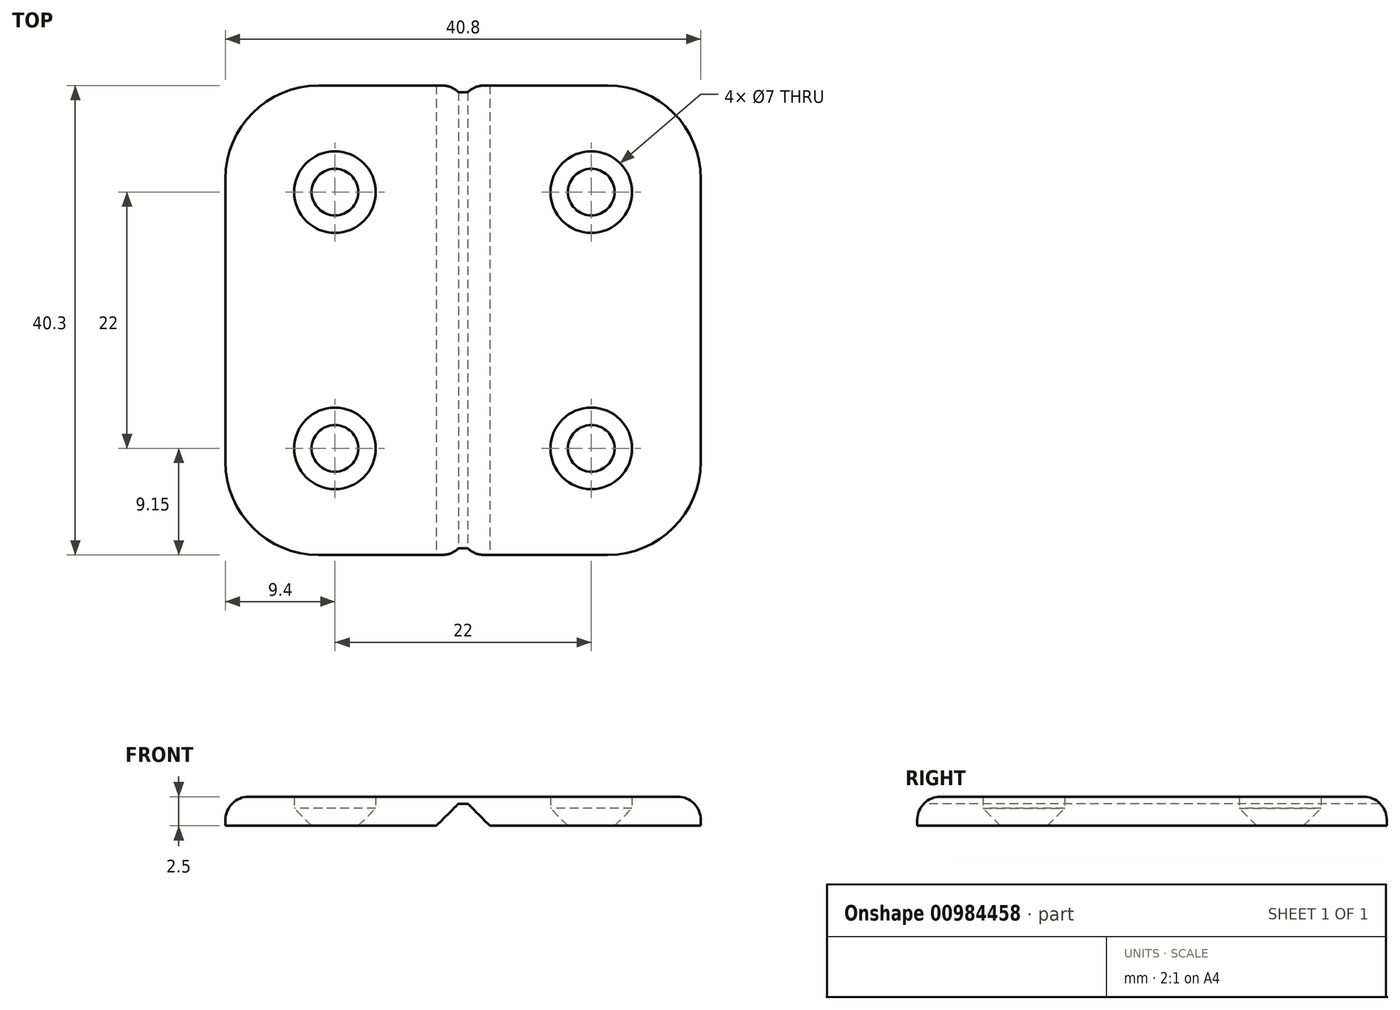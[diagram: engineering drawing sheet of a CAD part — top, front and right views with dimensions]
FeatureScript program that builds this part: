
annotation { "Feature Type Name" : "Feature", "Feature Type Description" : "" }
export const myFeature = defineFeature(function(context is Context, id is Id, definition is map)
    precondition{}
    {
        {
            var Q0;
            Q0=qCreatedBy(makeId("Top.planeOp"),FACE);
            var sketch = newSketch(context, id + "F0", { "sketchPlane" : qUnion([Q0])});
            skLineSegment(sketch, "E0.bottom", {"start": v(12.4, 20.15) * mm, "end": v(-12.4, 20.15) * mm});
            skLineSegment(sketch, "E0.top", {"start": v(12.4, -20.15) * mm, "end": v(-12.4, -20.15) * mm});
            skLineSegment(sketch, "E0.left", {"start": v(20.4, 12.15) * mm, "end": v(20.4, -12.15) * mm});
            skLineSegment(sketch, "E0.right", {"start": v(-20.4, 12.15) * mm, "end": v(-20.4, -12.15) * mm});
            skPoint(sketch, "E0.middle", {"position": v(0, 0) * mm});
            skPoint(sketch, "E1.visualSharp", {"position": v(-20.4, 20.15) * mm});
            skArc(sketch, "E1.filletArc", {"start": v(-12.4, 20.15) * mm, "mid": v(-18.06, 17.8) * mm, "end": v(-20.4, 12.15) * mm});
            skPoint(sketch, "E2.visualSharp", {"position": v(20.4, 20.15) * mm});
            skArc(sketch, "E2.filletArc", {"start": v(20.4, 12.15) * mm, "mid": v(18.06, 17.8) * mm, "end": v(12.4, 20.15) * mm});
            skPoint(sketch, "E3.visualSharp", {"position": v(20.4, -20.15) * mm});
            skArc(sketch, "E3.filletArc", {"start": v(12.4, -20.15) * mm, "mid": v(18.06, -17.8) * mm, "end": v(20.4, -12.15) * mm});
            skPoint(sketch, "E4.visualSharp", {"position": v(-20.4, -20.15) * mm});
            skArc(sketch, "E4.filletArc", {"start": v(-20.4, -12.15) * mm, "mid": v(-18.06, -17.8) * mm, "end": v(-12.4, -20.15) * mm});
            skCircle(sketch, "E5", {"center": v(11, 11) * mm, "radius": 2 * mm});
            skCircle(sketch, "E6", {"center": v(11, -11) * mm, "radius": 2 * mm});
            skCircle(sketch, "E7", {"center": v(-11, -11) * mm, "radius": 2 * mm});
            skCircle(sketch, "E8", {"center": v(-11, 11) * mm, "radius": 2 * mm});
            skCircle(sketch, "E9", {"center": v(-11, 11) * mm, "radius": 3.5 * mm});
            skCircle(sketch, "E10", {"center": v(11, 11) * mm, "radius": 3.5 * mm});
            skCircle(sketch, "E11", {"center": v(-11, -11) * mm, "radius": 3.5 * mm});
            skCircle(sketch, "E12", {"center": v(11, -11) * mm, "radius": 3.5 * mm});
            skSolve(sketch);
        }
        {
            var Q0;
            Q0=makeQuery(id+"F0.imprint","IMPRINT",FACE,{"disambiguationData":[TD([[makeQuery(id+"F0.imprint","IMPRINT",EDGE,{"derivedFrom":sQuery(id+"F0.wireOp",EDGE,"E0.bottom")}),1.0]])]});
            var Q1;
            Q1=makeQuery(id+"F0.imprint","IMPRINT",FACE,{"disambiguationData":[TD([[makeQuery(id+"F0.imprint","IMPRINT",EDGE,{"derivedFrom":sQuery(id+"F0.wireOp",EDGE,"E8")}),-1.0]])]});
            var Q2;
            Q2=makeQuery(id+"F0.imprint","IMPRINT",FACE,{"disambiguationData":[TD([[makeQuery(id+"F0.imprint","IMPRINT",EDGE,{"derivedFrom":sQuery(id+"F0.wireOp",EDGE,"E5")}),-1.0]])]});
            var Q3;
            Q3=makeQuery(id+"F0.imprint","IMPRINT",FACE,{"disambiguationData":[TD([[makeQuery(id+"F0.imprint","IMPRINT",EDGE,{"derivedFrom":sQuery(id+"F0.wireOp",EDGE,"E6")}),-1.0]])]});
            var Q4;
            Q4=makeQuery(id+"F0.imprint","IMPRINT",FACE,{"disambiguationData":[TD([[makeQuery(id+"F0.imprint","IMPRINT",EDGE,{"derivedFrom":sQuery(id+"F0.wireOp",EDGE,"E7")}),-1.0]])]});
            extrude(context, id + "F1", {"entities" : qUnion([Q0, Q1, Q2, Q3, Q4]), "depth" : 1.5 * mm, "offsetDistance" : 25 * mm});
        }
        {
            var Q0;
            Q0=makeQuery(id+"F0.imprint","IMPRINT",FACE,{"disambiguationData":[TD([[makeQuery(id+"F0.imprint","IMPRINT",EDGE,{"derivedFrom":sQuery(id+"F0.wireOp",EDGE,"E0.bottom")}),1.0]])]});
            extrude(context, id + "F2", {"entities" : qUnion([Q0]), "operationType" : NewBodyOperationType.ADD, "depth" : 2.5 * mm, "offsetDistance" : 25 * mm});
        }
        {
            var Q0;
            Q0=makeQuery(id+"F2.opExtrude","CAP_EDGE",EDGE,{"disambiguationData":[OSD([sQuery(id+"F0.wireOp",EDGE,"E1.filletArc")])],"isStart":false});
            fillet(context, id + "F3", {"entities" : qUnion([Q0]), "radius" : 2 * mm, "tangentPropagation" : true, "allowEdgeOverflow" : false});
        }
        {
            var Q0;
            Q0=makeQuery(id+"F1.opExtrude","CAP_EDGE",EDGE,{"disambiguationData":[OSD([sQuery(id+"F0.wireOp",EDGE,"E8")])],"isStart":false});
            var Q1;
            Q1=makeQuery(id+"F1.opExtrude","CAP_EDGE",EDGE,{"disambiguationData":[OSD([sQuery(id+"F0.wireOp",EDGE,"E5")])],"isStart":false});
            var Q2;
            Q2=makeQuery(id+"F1.opExtrude","CAP_EDGE",EDGE,{"disambiguationData":[OSD([sQuery(id+"F0.wireOp",EDGE,"E6")])],"isStart":false});
            var Q3;
            Q3=makeQuery(id+"F1.opExtrude","CAP_EDGE",EDGE,{"disambiguationData":[OSD([sQuery(id+"F0.wireOp",EDGE,"E7")])],"isStart":false});
            chamfer(context, id + "F4", {"entities" : qUnion([Q0, Q1, Q2, Q3]), "width" : 1.5 * mm, "tangentPropagation" : true});
        }
        {
            var Q0;
            {var subQ0=sQuery(id+"F0.wireOp",EDGE,"E0.top");Q0=makeQuery(id+"F2.boolean.opBoolean","MERGE",FACE,{"derivedFrom":[makeQuery(id+"F1.opExtrude","SWEPT_FACE",FACE,{"disambiguationData":[OSD([subQ0])]}),makeQuery(id+"F2.opExtrude","SWEPT_FACE",FACE,{"disambiguationData":[OSD([subQ0])]})]});}
            cPlane(context, id + "F5", {"entities" : qUnion([Q0]), "cplaneType" : CPlaneType.OFFSET, "offset" : 0 * mm, "width" : 150 * mm, "height" : 150 * mm});
        }
        {
            var Q0;
            Q0=qCreatedBy(id+"F5.planeOp",FACE);
            var sketch = newSketch(context, id + "F6", { "sketchPlane" : qUnion([Q0])});
            skLineSegment(sketch, "E13.0.0", {"start": v(-12.4, 2.5) * mm, "end": v(-12.4, 0.5) * mm});
            skLineSegment(sketch, "E13.0.2", {"start": v(12.4, 0.5) * mm, "end": v(12.4, 2.5) * mm});
            skLineSegment(sketch, "E13.0.3", {"start": v(-12.4, 2.5) * mm, "end": v(12.4, 2.5) * mm, "construction": true});
            skLineSegment(sketch, "E14.0.0", {"start": v(12.4, 0) * mm, "end": v(12.4, 0.5) * mm});
            skLineSegment(sketch, "E14.0.2", {"start": v(-12.4, 0.5) * mm, "end": v(-12.4, 0) * mm});
            skLineSegment(sketch, "E14.0.3", {"start": v(-12.4, 0) * mm, "end": v(12.4, 0) * mm});
            skLineSegment(sketch, "E15", {"start": v(0.4, 7.15) * mm, "end": v(0.4, -5) * mm, "construction": true});
            skLineSegment(sketch, "E16", {"start": v(-0.4, -5) * mm, "end": v(-0.4, 7.44) * mm, "construction": true});
            skLineSegment(sketch, "E17", {"start": v(-10.47, 1.9) * mm, "end": v(10.6, 1.9) * mm, "construction": true});
            skLineSegment(sketch, "E18", {"start": v(-2.3, 5.8) * mm, "end": v(-2.3, -4.07) * mm, "construction": true});
            skLineSegment(sketch, "E19", {"start": v(2.3, -4.14) * mm, "end": v(2.3, 6) * mm, "construction": true});
            skLineSegment(sketch, "E20", {"start": v(-2.3, 0) * mm, "end": v(-0.4, 1.9) * mm});
            skPoint(sketch, "E20.endSnap0", {"position": v(0.07, 1.9) * mm});
            skLineSegment(sketch, "E21", {"start": v(-0.4, 1.9) * mm, "end": v(0.4, 1.9) * mm});
            skLineSegment(sketch, "E22", {"start": v(0.4, 1.9) * mm, "end": v(2.3, 0) * mm});
            skLineSegment(sketch, "E23", {"start": v(2.3, 0) * mm, "end": v(-2.3, 0) * mm});
            skSolve(sketch);
        }
        {
            var Q0;
            Q0=makeQuery(id+"F6.imprint","IMPRINT",FACE,{"disambiguationData":[TD([[makeQuery(id+"F6.imprint","IMPRINT",EDGE,{"derivedFrom":sQuery(id+"F6.wireOp",EDGE,"E20")}),-1.0]])]});
            extrude(context, id + "F7", {"entities" : qUnion([Q0]), "operationType" : NewBodyOperationType.REMOVE, "endBound" : BoundingType.THROUGH_ALL, "oppositeDirection" : true, "depth" : 25 * mm, "offsetDistance" : 25 * mm});
        }
    });
